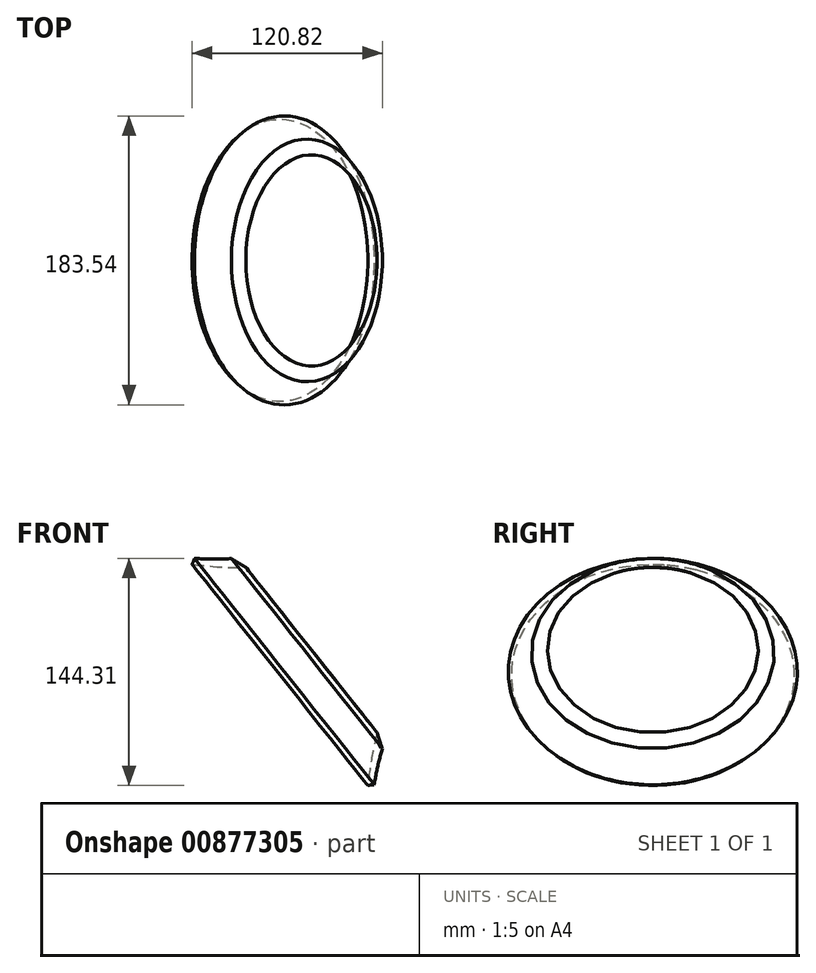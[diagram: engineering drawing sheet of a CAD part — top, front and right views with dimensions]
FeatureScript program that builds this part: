
annotation { "Feature Type Name" : "Feature", "Feature Type Description" : "" }
export const myFeature = defineFeature(function(context is Context, id is Id, definition is map)
    precondition{}
    {
        {
            var Q0;
            Q0=qCreatedBy(makeId("Front.planeOp"),FACE);
            var sketch = newSketch(context, id + "F0", { "sketchPlane" : qUnion([Q0])});
            skLineSegment(sketch, "E0", {"start": v(-57.87, 52.72) * mm, "end": v(-39.74, 67.12) * mm});
            skLineSegment(sketch, "E1", {"start": v(-57.87, 7.2) * mm, "end": v(-39.74, -0.11) * mm});
            skLineSegment(sketch, "E2", {"start": v(-39.74, 67.12) * mm, "end": v(-39.74, -0.11) * mm});
            skLineSegment(sketch, "E3", {"start": v(-57.87, 52.72) * mm, "end": v(-57.87, 7.2) * mm});
            skSolve(sketch);
        }
        {
            var Q0;
            Q0=qCreatedBy(makeId("Right.planeOp"),FACE);
            var sketch = newSketch(context, id + "F1", { "sketchPlane" : qUnion([Q0])});
            skLineSegment(sketch, "E4", {"start": v(64.46, 15.27) * mm, "end": v(56.42, 9.62) * mm});
            skLineSegment(sketch, "E5", {"start": v(64.46, 15.27) * mm, "end": v(64.46, 44.74) * mm});
            skLineSegment(sketch, "E6", {"start": v(64.46, 44.74) * mm, "end": v(55.48, 50.65) * mm});
            skLineSegment(sketch, "E7", {"start": v(56.42, 9.62) * mm, "end": v(55.48, 50.65) * mm});
            skSolve(sketch);
        }
        {
            var Q0;
            Q0 = qSketchRegion(id + "F1", true);
            var Q1;
            Q1=sQuery(id+"F0.wireOp",EDGE,"E0");
            revolve(context, id + "F2", {"surfaceOperationType" : NewSurfaceOperationType.NEW, "entities" : qUnion([Q0]), "axis" : qUnion([Q1]), "revolveType" : RevolveType.FULL});
        }
    });
